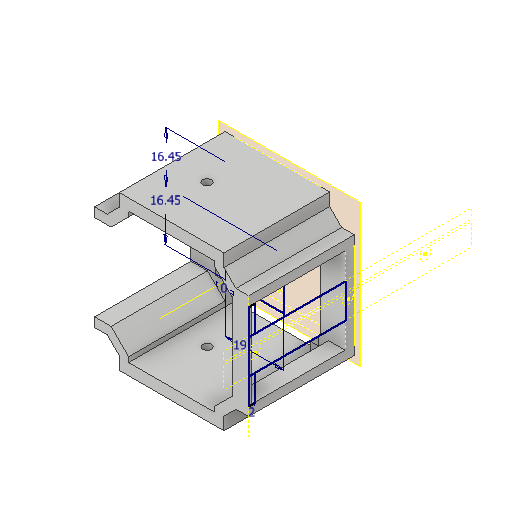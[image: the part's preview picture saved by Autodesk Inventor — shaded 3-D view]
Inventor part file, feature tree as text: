
AUTODESK INVENTOR PART (.ipt)
format: ipt  version: 2022 (Build 260153000, 153)  size: 359,424 bytes
history: native  units: mm
features: reference x17, other x12, sketch x7, projected_geometry x7, extrude x6, plane x4, chamfer x1, pattern_circular x1
ambient origin geometry x8: Origin, YZ Plane, XZ Plane, XY Plane, X Axis, Y Axis, Z Axis, Center Point
bodies: Solid1 (feature_tree)
feature tree (55):
  plane  "Work Plane1"
  extrude  "Extrusion1"  Depth=0.1mm
  chamfer  "Chamfer1"  Distance=3.0mm
  sketch  "Sketch2"  dims[d3=0.1mm]
  plane  "Work Plane2"
  extrude  "Extrusion2"  Depth=3.001102mm
  other  "Work Axis1"
  pattern_circular  "Circular Pattern1"  [2 undecoded]
  extrude  "Extrusion3"  Depth=3.7mm TaperAngle=360.0deg
  sketch  "Sketch4"  dims[d5=0.1mm]
  plane  "Work Plane3"
  sketch  "Sketch7"  dims[d6=3.0mm]
  plane  "Work Plane4"
  other  "Work Point1"
  extrude  "Extrusion12"  Depth=3.7mm
  extrude  "Extrusion13"  Depth=1.0mm TaperAngle=0.0deg
  extrude  "Extrusion14"  Depth=3.7mm
  sketch  "Sketch1"  dims[d1=0.1mm d2=0.1mm]
  reference  "Reference1"
  reference  "Reference2"
  reference  "Reference3"
  reference  "Reference4"
  reference  "Reference5"
  reference  "Reference6"
  reference  "Reference7"
  projected_geometry  "Projected Loop1"
  sketch  "Sketch3"  dims[d4=0.1mm]
  reference  "Reference8"
  projected_geometry  "Projected Loop2"
  projected_geometry  "Projected Loop3"
  reference  "Reference9"
  reference  "Reference10"
  reference  "Reference11"
  reference  "Reference13"
  reference  "Reference14"
  reference  "Reference15"
  reference  "Reference16"
  projected_geometry  "Projected Loop5"
  reference  "Reference22"
  projected_geometry  "Projected Loop8"
  reference  "Reference28"
  sketch  "Sketch15"  dims[d7=3.0mm d8=3.0mm d9=0.0mm]
  projected_geometry  "Projected Loop9"
  sketch  "Sketch16"  dims[d10=3.9mm d11=2.0mm d12=45.0deg d13=3.001102mm d14=6.0mm d15=0.0mm d16=40.0mm d17=360.0deg d19=6.0mm d20=1.0mm d21=0.0mm d24=2.0mm d35=19.0mm d36=0.0mm d74=16.45mm d75=16.45mm d82=10.0mm d83=0.0mm d87=10.0mm d88=0.0mm d89=2.8mm d90=3.7mm d91=0.0mm]
  projected_geometry  "Projected Loop10"
  other  "Assembly_Cube_Z_Focus_MGN_NEMA_v3.iam"
  other  "00_MGN12 LINEAR GUIDE RAIL, CONFIGURABLE:1"
  other  "<userpath>\Documents\UC2-INVENTOR-Git\uc2_v3\Assembly_Cube_Z_Focus_MGN_manual_v3.iam"
  other  "Assembly_Cube_Z_Focus_MGN_manual_v3.iam"
  other  "Assembly_Cube_empty_IM_v3:1"
  other  "10_Cube_1x1_IM:2"
  other  "10_Cube_1x1_IM:1"
  other  "00_NEMA11:1"
  other  "DIN 912 - replaced by DIN EN ISO 4762 M3 x 30:1"
  other  "30_Cube_Z_Focus_MGN12_manual_gear_v3:1"
note: 2 required parameter values undecoded (feature->parameter linkage not recoverable at this tier; creation-order binding heuristic only, values carry confidence <= 0.55)
